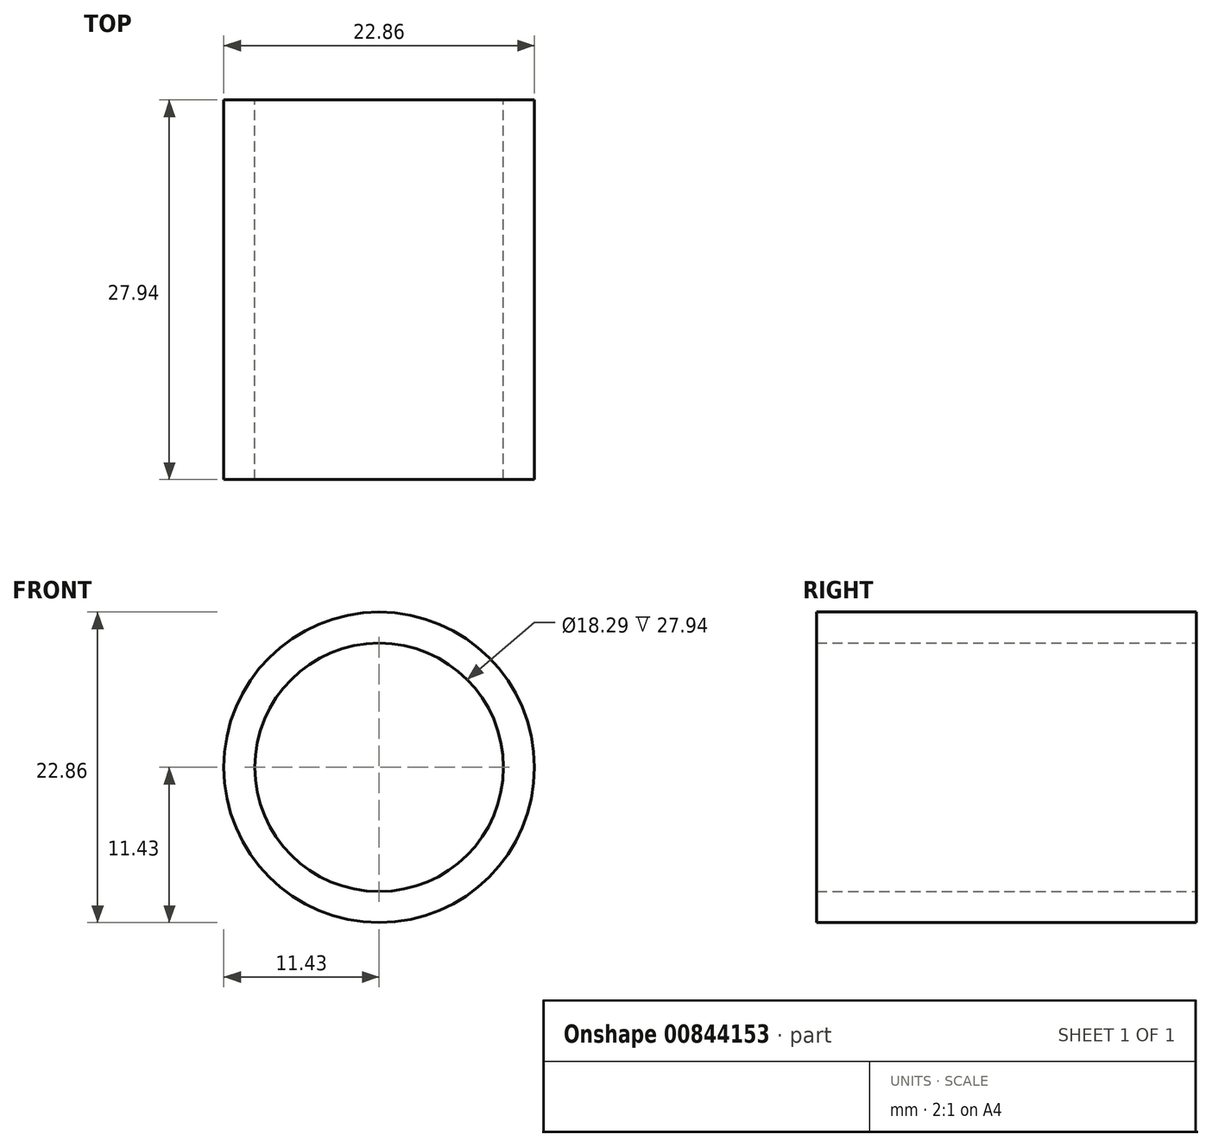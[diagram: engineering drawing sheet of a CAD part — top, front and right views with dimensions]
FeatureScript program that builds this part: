
annotation { "Feature Type Name" : "Feature", "Feature Type Description" : "" }
export const myFeature = defineFeature(function(context is Context, id is Id, definition is map)
    precondition{}
    {
        {
            var Q0;
            Q0=qCreatedBy(makeId("Front.planeOp"),FACE);
            var sketch = newSketch(context, id + "F0", { "sketchPlane" : qUnion([Q0])});
            skCircle(sketch, "E0", {"center": v(0, 0) * mm, "radius": 9.14 * mm});
            skCircle(sketch, "E1", {"center": v(0, 0) * mm, "radius": 11.43 * mm});
            skSolve(sketch);
        }
        {
            var Q0;
            Q0=makeQuery(id+"F0.imprint","IMPRINT",FACE,{"disambiguationData":[TD([[makeQuery(id+"F0.imprint","IMPRINT",EDGE,{"derivedFrom":sQuery(id+"F0.wireOp",EDGE,"E0")}),-1.0]])]});
            extrude(context, id + "F1", {"entities" : qUnion([Q0]), "depth" : 21.59 * mm, "offsetDistance" : 25.4 * mm, "hasSecondDirection" : true, "secondDirectionOppositeDirection" : true, "secondDirectionDepth" : 6.35 * mm});
        }
    });
